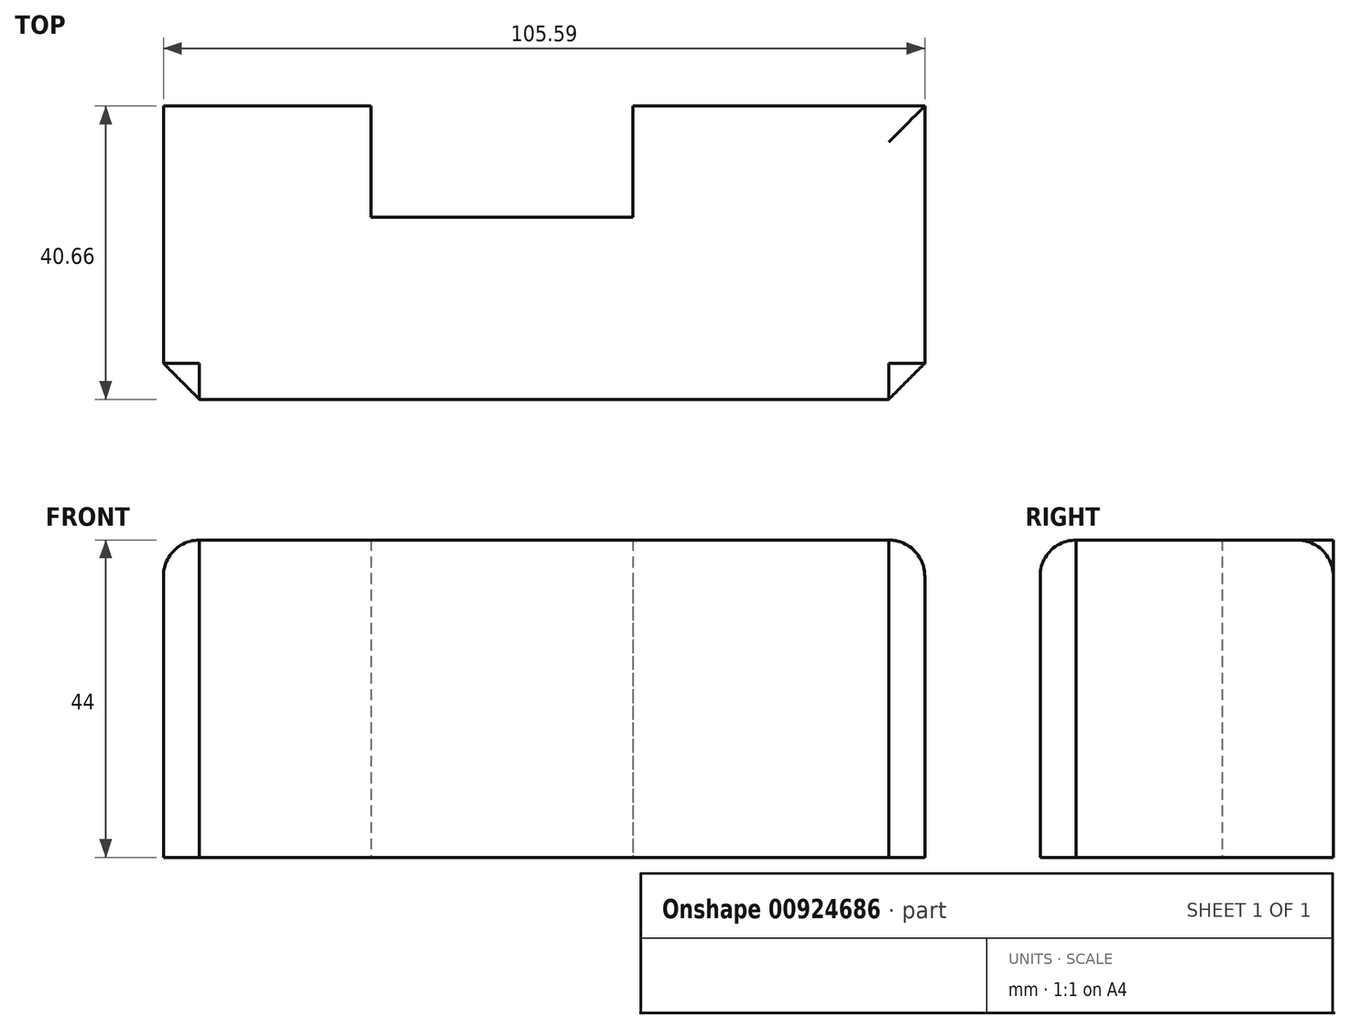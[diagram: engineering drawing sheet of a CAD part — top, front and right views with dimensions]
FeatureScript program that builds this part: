
annotation { "Feature Type Name" : "Feature", "Feature Type Description" : "" }
export const myFeature = defineFeature(function(context is Context, id is Id, definition is map)
    precondition{}
    {
        {
            var Q0;
            Q0=qCreatedBy(makeId("Top.planeOp"),FACE);
            var sketch = newSketch(context, id + "F0", { "sketchPlane" : qUnion([Q0])});
            skLineSegment(sketch, "E0.bottom", {"start": v(-65.13, 10.36) * mm, "end": v(40.46, 10.36) * mm});
            skLineSegment(sketch, "E0.top", {"start": v(-65.13, -30.3) * mm, "end": v(40.46, -30.3) * mm});
            skLineSegment(sketch, "E0.left", {"start": v(-65.13, 10.36) * mm, "end": v(-65.13, -30.3) * mm});
            skLineSegment(sketch, "E0.right", {"start": v(40.46, 10.36) * mm, "end": v(40.46, -30.3) * mm});
            skLineSegment(sketch, "E1", {"start": v(-36.33, 10.36) * mm, "end": v(-36.33, -5.06) * mm});
            skLineSegment(sketch, "E2", {"start": v(-36.33, -5.06) * mm, "end": v(0, -5.06) * mm});
            skLineSegment(sketch, "E3", {"start": v(0, -5.06) * mm, "end": v(0, 10.36) * mm});
            skSolve(sketch);
        }
        {
            var Q0;
            Q0=makeQuery(id+"F0.imprint","IMPRINT",FACE,{"disambiguationData":[TD([[makeQuery(id+"F0.imprint","IMPRINT",EDGE,{"derivedFrom":sQuery(id+"F0.wireOp",EDGE,"E0.top")}),1.0]])]});
            extrude(context, id + "F1", {"entities" : qUnion([Q0]), "depth" : 44 * mm, "offsetDistance" : 25 * mm});
        }
        {
            var Q0;
            Q0=makeQuery(id+"F1.opExtrude","CAP_EDGE",EDGE,{"disambiguationData":[OSD([sQuery(id+"F0.wireOp",EDGE,"E0.top")])],"isStart":false});
            var Q1;
            Q1=makeQuery(id+"F1.opExtrude","CAP_EDGE",EDGE,{"disambiguationData":[OSD([sQuery(id+"F0.wireOp",EDGE,"E0.right")])],"isStart":false});
            var Q2;
            {var subQ0=sQuery(id+"F0.wireOp",EDGE,"E0.bottom");Q2=makeQuery(id+"F1.opExtrude","CAP_EDGE",EDGE,{"disambiguationData":[OSD([subQ0]),TDD([makeQuery(id+"F0.imprint","IMPRINT",EDGE,{"disambiguationData":[TD([[makeQuery(id+"F0.imprint","INTERSECT",VERTEX,{"derivedFrom":[subQ0,sQuery(id+"F0.wireOp",EDGE,"E0.right")]}),1.0]])],"derivedFrom":subQ0})])],"isStart":false});}
            var Q3;
            Q3=makeQuery(id+"F1.opExtrude","CAP_EDGE",EDGE,{"disambiguationData":[OSD([sQuery(id+"F0.wireOp",EDGE,"E0.left")])],"isStart":false});
            fillet(context, id + "F2", {"entities" : qUnion([Q0, Q1, Q2, Q3]), "radius" : 5 * mm, "tangentPropagation" : true, "allowEdgeOverflow" : false});
        }
        {
            var Q0;
            Q0=makeQuery(id+"F1.opExtrude","SWEPT_EDGE",EDGE,{"disambiguationData":[OSD([sQuery(id+"F0.wireOp",EDGE,"E0.top"),sQuery(id+"F0.wireOp",EDGE,"E0.right")])]});
            var Q1;
            Q1=makeQuery(id+"F1.opExtrude","SWEPT_EDGE",EDGE,{"disambiguationData":[OSD([sQuery(id+"F0.wireOp",EDGE,"E0.top"),sQuery(id+"F0.wireOp",EDGE,"E0.left")])]});
            chamfer(context, id + "F3", {"entities" : qUnion([Q0, Q1]), "width" : 5 * mm, "tangentPropagation" : true});
        }
    });
